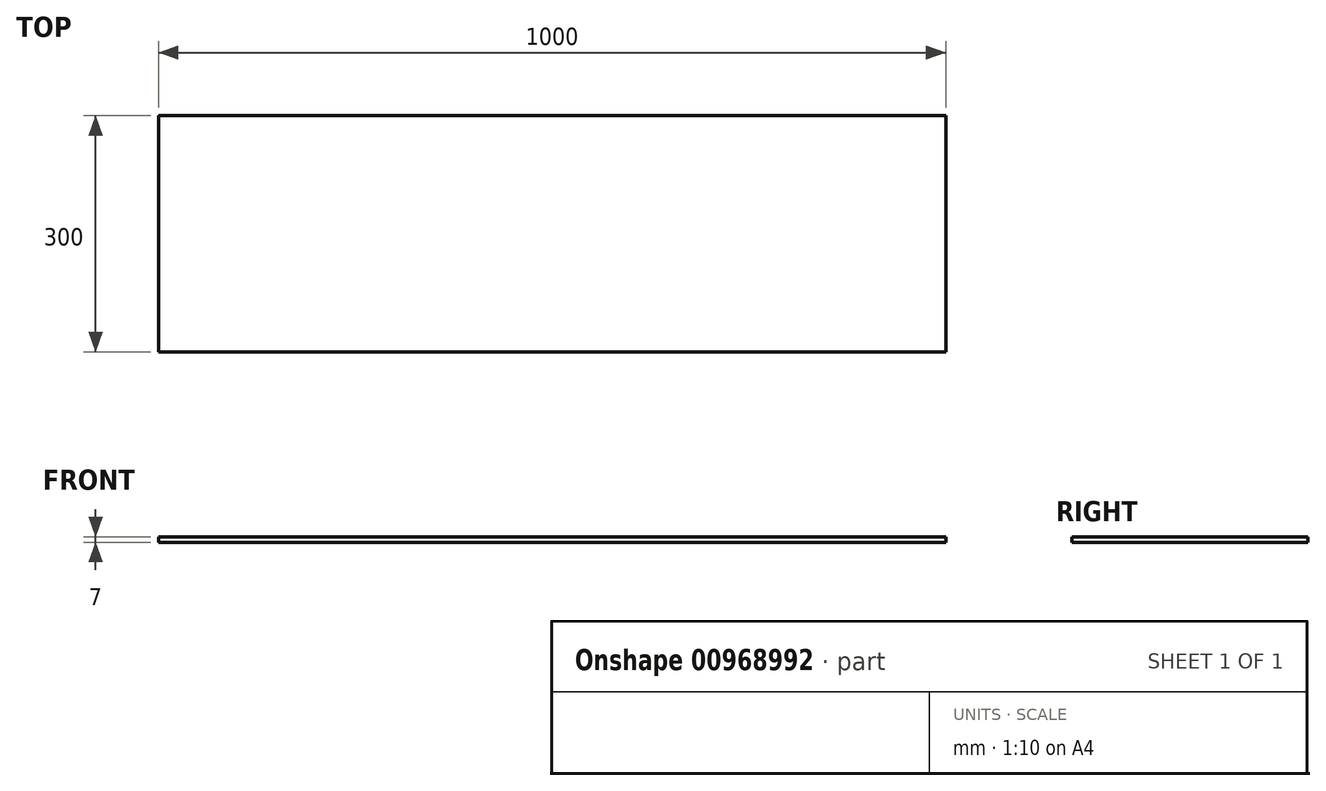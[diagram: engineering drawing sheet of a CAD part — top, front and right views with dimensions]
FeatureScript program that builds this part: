
annotation { "Feature Type Name" : "Feature", "Feature Type Description" : "" }
export const myFeature = defineFeature(function(context is Context, id is Id, definition is map)
    precondition{}
    {
        {
            var Q0;
            Q0=qCreatedBy(makeId("Top.planeOp"),FACE);
            var sketch = newSketch(context, id + "F0", { "sketchPlane" : qUnion([Q0])});
            skLineSegment(sketch, "E0.bottom", {"start": v(500, 150) * mm, "end": v(-500, 150) * mm});
            skLineSegment(sketch, "E0.top", {"start": v(500, -150) * mm, "end": v(-500, -150) * mm});
            skLineSegment(sketch, "E0.left", {"start": v(500, 150) * mm, "end": v(500, -150) * mm});
            skLineSegment(sketch, "E0.right", {"start": v(-500, 150) * mm, "end": v(-500, -150) * mm});
            skPoint(sketch, "E0.middle", {"position": v(0, 0) * mm});
            skSolve(sketch);
        }
        {
            var Q0;
            Q0=makeQuery(id+"F0.imprint","IMPRINT",FACE,{"disambiguationData":[TD([[makeQuery(id+"F0.imprint","IMPRINT",EDGE,{"derivedFrom":sQuery(id+"F0.wireOp",EDGE,"E0.bottom")}),1.0]])]});
            extrude(context, id + "F1", {"entities" : qUnion([Q0]), "depth" : 7 * mm, "offsetDistance" : 25 * mm});
        }
    });
